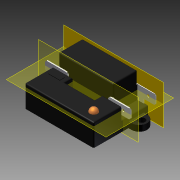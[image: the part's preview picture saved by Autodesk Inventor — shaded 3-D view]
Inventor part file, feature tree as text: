
AUTODESK INVENTOR PART (.ipt)
format: ipt  version: 2011 (Build 150239000, 239)  size: 304,128 bytes
history: native  units: mm (DEFAULTED — no unit token found)
features: plane x3, other x1, fillet x1, imported_body x1
ambient origin geometry x8: Origin, YZ Plane, XZ Plane, XY Plane, X Axis, Y Axis, Z Axis, Center Point
bodies: Solid1 (feature_tree)
feature tree (6):
  other  "Spike Relay.ipt"
  fillet  "Fillet1"  Radius=0.762mm
  plane  "Work Plane1"
  plane  "Work Plane2"
  plane  "Work Plane3"
  imported_body  "DerivedBody::Spike Relay.ipt"
